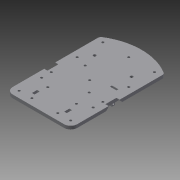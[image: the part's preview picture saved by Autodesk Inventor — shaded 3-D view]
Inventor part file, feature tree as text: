
AUTODESK INVENTOR PART (.ipt)
format: ipt  version: 2015 (Build 190159000, 159)  size: 502,272 bytes
history: native  units: mm
features: extrude x14, sketch x14, fillet x4, hole x1, chamfer x1
ambient origin geometry x8: Origin, YZ Plane, XZ Plane, XY Plane, X Axis, Y Axis, Z Axis, Center Point
bodies: Volumenkörper1 (feature_tree)
feature tree (34):
  extrude  "Extrusion1"  Depth=100.0mm
  fillet  "Rundung2"  Radius=5.0mm
  fillet  "Rundung3"  Radius=10.0mm
  extrude  "Extrusion2"  Depth=5.0mm
  extrude  "Extrusion3"  Depth=3.5mm
  extrude  "Extrusion4"  Depth=3.5mm
  extrude  "Extrusion5"  Depth=3.5mm
  fillet  "Rundung4"  Radius=3.5mm
  extrude  "Extrusion6"  Depth=3.5mm
  extrude  "Extrusion7"  Depth=140.0mm
  hole  "Bohrung1"  [1 undecoded]
  extrude  "Extrusion8"  Depth=100.0mm
  extrude  "Extrusion9"  Depth=60.0mm
  extrude  "Extrusion10"  Depth=10.0mm
  extrude  "Extrusion11"  Depth=10.0mm
  extrude  "Extrusion12"  Depth=90.0mm
  extrude  "Extrusion13"  Depth=10.0mm
  fillet  "Rundung7"  Radius=90.0mm
  extrude  "Extrusion14"  Depth=10.0mm
  chamfer  "Fase1"  Distance=90.0mm
  sketch  "Skizze1"  dims[d0=145.0mm d1=100.0mm d2=5.0mm d3=0.0mm d10=10.0mm]
  sketch  "Skizze3"  dims[d11=5.0mm d12=3.5mm]
  sketch  "Skizze4"  dims[d13=3.5mm d14=3.5mm]
  sketch  "Skizze5"  dims[d15=3.5mm d16=3.5mm]
  sketch  "Skizze6"  dims[d17=3.5mm d18=3.5mm d19=3.5mm]
  sketch  "Skizze7"  dims[d20=3.5mm d21=3.5mm]
  sketch  "Skizze8"  dims[d22=3.5mm d23=140.0mm]
  sketch  "Skizze9"  dims[d24=140.0mm d25=140.0mm]
  sketch  "Skizze10"  dims[d26=100.0mm d27=100.0mm]
  sketch  "Skizze11"  dims[d28=60.0mm d29=60.0mm]
  sketch  "Skizze12"  dims[d30=10.0mm d31=10.0mm]
  sketch  "Skizze13"  dims[d32=10.0mm d33=10.0mm]
  sketch  "Skizze14"  dims[d34=90.0mm d35=70.0mm]
  sketch  "Skizze15"  dims[d36=30.0mm d37=10.0mm d38=90.0mm d39=10.0mm d40=90.0mm d41=10.0mm d42=90.0mm d43=50.0mm d44=10.0mm d45=6.0mm d46=0.0mm d49=5.7mm d50=5.7mm d51=5.7mm d52=5.7mm d53=5.7mm d54=5.7mm d55=5.7mm d56=5.7mm d57=5.7mm d58=5.7mm d59=5.7mm d60=4.3mm d61=0.0mm d62=4.3mm d63=4.3mm d64=116.0mm d65=116.0mm d66=21.5mm d67=57.25mm d68=21.25mm d69=3.0mm d70=0.0mm d71=10.0mm d72=50.0mm d73=152.5mm d74=22.0mm d75=0.0mm d76=5.0mm d77=5.0mm d78=5.0mm d79=5.0mm d80=5.0mm d81=5.0mm d82=5.0mm d83=10.0mm d84=10.0mm d85=42.5mm d86=42.5mm d87=79.5mm d88=79.5mm d89=23.0mm d90=23.0mm d91=15.6mm d92=15.6mm d93=23.0mm d94=0.0mm d95=2.5mm d97=20.0mm d98=3.5mm d99=3.5mm d100=5.0mm d101=23.0mm d102=0.0mm d103=2.5mm d113=11.5mm d105=3.0mm d106=6.0mm d107=4.0mm d108=2.0mm d109=90.0deg d110=8.0mm d111=20.594885mm d114=23.0mm d115=0.0mm d116=2.5mm d124=3.5mm d125=3.5mm d126=10.0mm d127=90.0mm d128=45.0mm d129=45.0mm d130=10.0mm d131=0.0mm d132=5.7mm d133=5.7mm d134=4.3mm d135=0.0mm d136=4.0mm d137=4.0mm d138=3.0mm d139=10.0mm d140=8.0mm d141=8.0mm d142=17.0mm d143=17.0mm d144=23.0mm d145=23.0mm d146=15.0mm d147=86.0mm d148=3.0mm d149=0.0mm d150=3.5mm d151=3.5mm d152=3.5mm d156=27.5mm d157=37.0mm d158=37.0mm d159=3.5mm d160=3.5mm d162=27.5mm d165=10.0mm d166=0.0mm d167=5.7mm d168=5.7mm d169=5.7mm d170=5.7mm d171=5.7mm d172=4.3mm d173=0.0mm d174=44.5mm d175=42.0mm d177=23.0mm d178=95.0mm d179=39.3mm d180=33.0mm d182=3.0mm d183=59.0mm d184=59.0mm d185=17.0mm d186=17.0mm d187=5.0mm d188=5.0mm d189=10.0mm d190=0.0mm d191=4.0mm d192=2.0mm d193=45.0deg]
note: 1 required parameter value undecoded (feature->parameter linkage not recoverable at this tier; creation-order binding heuristic only, values carry confidence <= 0.55)
